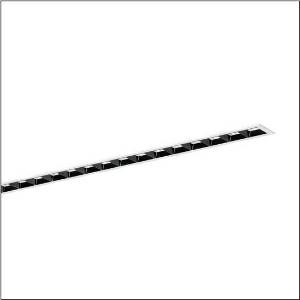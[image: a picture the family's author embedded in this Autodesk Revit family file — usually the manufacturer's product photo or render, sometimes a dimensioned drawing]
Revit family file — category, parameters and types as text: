
# Revit family: silica_21_51mx12dc4awb
name_source: partatom
category: Lighting Fixtures
units: mm (PartAtom-declared; Revit-internal decimal feet)

## family parameters
Cut with Voids When Loaded = No
Host = Face
Light Source = No
Part Type = Normal
Room Calculation Point = No
Round Connector Dimension = Use Diameter
Shared = No

## types (1)
- --- (1 x LED, 10800 lm, 64.7 W, 4000K)
    Apparent Load = 65 VA
    CIE Flux Codes = 86 100 100 100 100
    Color Rendering = 80
    Color Temperature = 4000K
    Default Elevation = 1800 mm
    Description = Silica 21, office luminaire, primary light control with darklight reflector, of PMMA, black, CAT 2 (L<= 3000cd/m²), light emission: direct distribution, primary light characteristic: symmetric, installation type: recessed, LED, rated luminous flux: 10.800lm, luminous efficacy: 167lm/W, light colour: 840, colour temperature: 4000K, control gear: DALI 2, with terminal, 3+2-pole, max. 2.5mm², mains connection: 220..240V, AC, 50/60Hz, rated input power: 64.7W, luminaire housing, of aluminium, traffic white (RAL 9016), length: 3.028mm, width: 79mm, height: 53mm, protection rating (complete): IP20, insulation class (complete): insulation class I (protective earthing), certification: CE, ENEC, VDE, permissible operating ambient temperature: 0..+35°C, standard: EN 50419, packaging unit: 1 piece
    Height = 0 mm  [stored 0 ft]
    Lamp = 1 x LED
    Lamp Light Flux = 10800 lm
    Lamp Power = 64.7 W
    Lamp count = 1
    Length = 3027 mm
    Luminous efficacy = 167 lm/W
    Manufacturer = Siteco
    ModVariant = No
    Model = 51MX12DC4AWB
    Mounting Place = Ceiling
    Mounting Type = Recessed
    Number of Poles = 1
    OnlyDefault = Yes
    Power Factor = 1
    Product Name = Silica 21
    Product group = office luminaire | ceiling recessed
    ProductGroupID = 400
    Protection Class = Protection class I
    Protection Degree = IP 20
    RLX_Detail_Level = 1
    RLX_Emergency_Light_Flux = 0 lm
    RLX_Emergency_Type = 0
    RLX_Emergency_Type_DB = No
    RlxData = <blob elided: 62705 chars, md5=f08a5cbc>
    Socket = socket
    Standby Power = 0 W
    System Light Flux = 10800 lm
    System Power = 65 W
    Type Comments = factory setting: luminous flux: 100 % | dim-lin: 254 | 366 mA
    Type Image = l_1335880.jpg
    URL = http://relux.com
    VarID = @adj_124545
    Voltage = 0 V
    Weight = 0.00 kg
    Width = 79 mm

note: [stored X ft] marks values corroborated as IEEE doubles in the binary element streams (Revit-internal decimal feet)

## geometry (parser evidence)
native form markers: Blend x4, Sweep x9
no freeform markers — native parametric forms only
